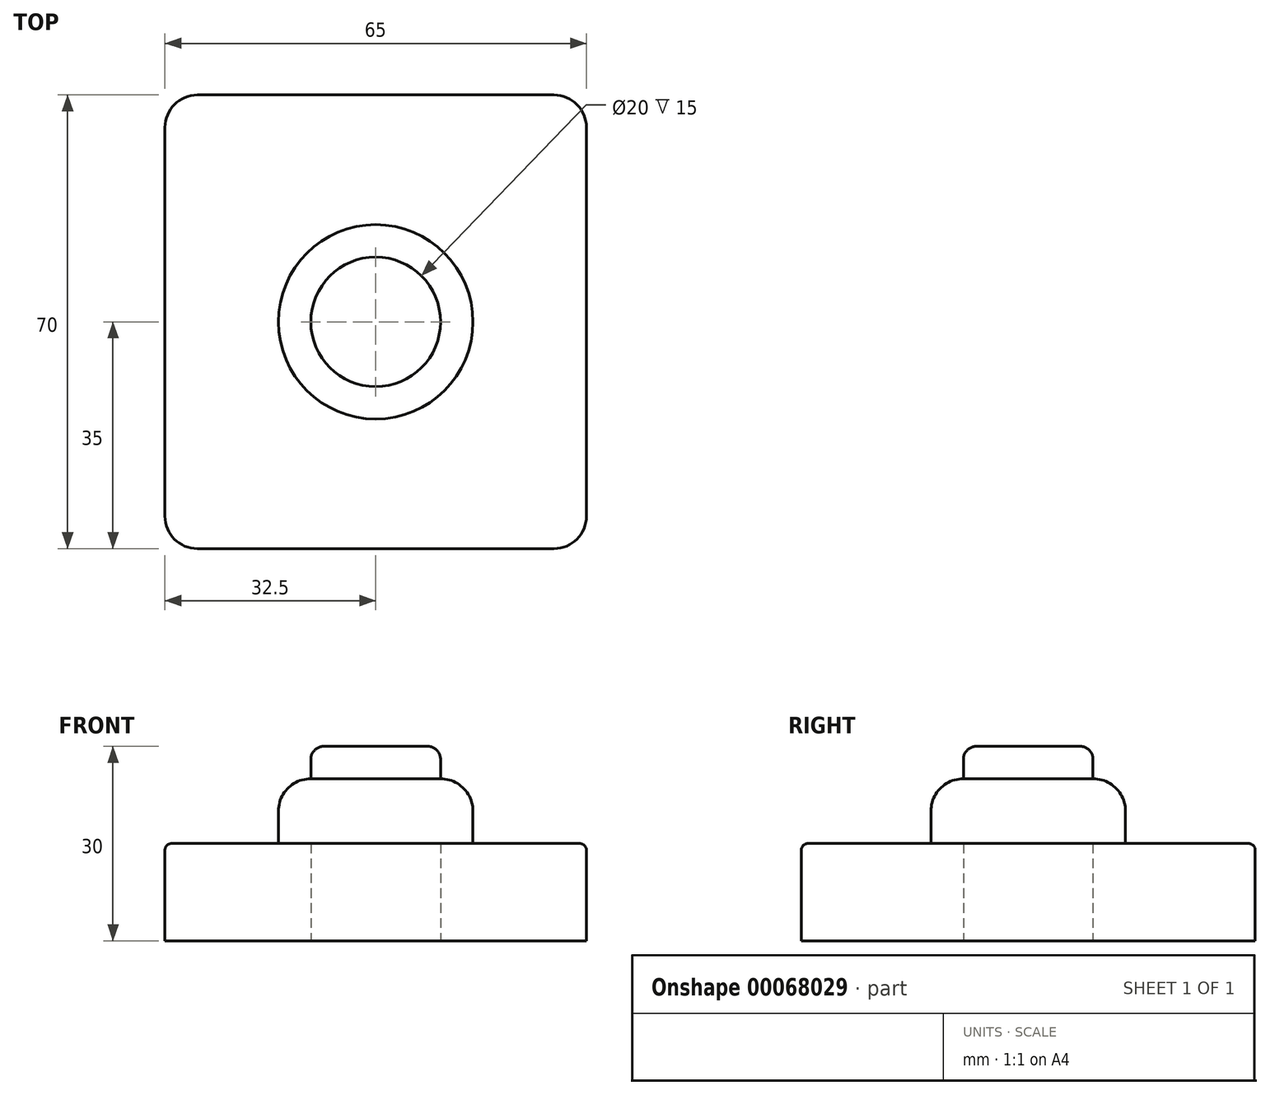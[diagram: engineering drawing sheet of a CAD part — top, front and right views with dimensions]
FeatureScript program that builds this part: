
annotation { "Feature Type Name" : "Feature", "Feature Type Description" : "" }
export const myFeature = defineFeature(function(context is Context, id is Id, definition is map)
    precondition{}
    {
        {
            var Q0;
            Q0=qCreatedBy(makeId("Top.planeOp"),FACE);
            var sketch = newSketch(context, id + "F0", { "sketchPlane" : qUnion([Q0])});
            skLineSegment(sketch, "E0.bottom", {"start": v(-27.5, 35) * mm, "end": v(27.5, 35) * mm});
            skLineSegment(sketch, "E0.top", {"start": v(-27.5, -35) * mm, "end": v(27.5, -35) * mm});
            skLineSegment(sketch, "E0.left", {"start": v(-32.5, 30) * mm, "end": v(-32.5, -30) * mm});
            skLineSegment(sketch, "E0.right", {"start": v(32.5, 30) * mm, "end": v(32.5, -30) * mm});
            skCircle(sketch, "E1", {"center": v(0, 0) * mm, "radius": 10 * mm});
            skPoint(sketch, "E2.visualSharp", {"position": v(-32.5, 35) * mm});
            skArc(sketch, "E2.filletArc", {"start": v(-27.5, 35) * mm, "mid": v(-31.04, 33.54) * mm, "end": v(-32.5, 30) * mm});
            skPoint(sketch, "E3.visualSharp", {"position": v(-32.5, -35) * mm});
            skArc(sketch, "E3.filletArc", {"start": v(-32.5, -30) * mm, "mid": v(-31.04, -33.54) * mm, "end": v(-27.5, -35) * mm});
            skPoint(sketch, "E4.visualSharp", {"position": v(32.5, -35) * mm});
            skArc(sketch, "E4.filletArc", {"start": v(27.5, -35) * mm, "mid": v(31.04, -33.54) * mm, "end": v(32.5, -30) * mm});
            skPoint(sketch, "E5.visualSharp", {"position": v(32.5, 35) * mm});
            skArc(sketch, "E5.filletArc", {"start": v(32.5, 30) * mm, "mid": v(31.04, 33.54) * mm, "end": v(27.5, 35) * mm});
            skSolve(sketch);
        }
        {
            var Q0;
            Q0 = qSketchRegion(id + "F0", true);
            extrude(context, id + "F1", {"entities" : qUnion([Q0]), "flatOperationType" : FlatOperationType.REMOVE, "depth" : 15 * mm, "offsetDistance" : 25 * mm, "domain" : OperationDomain.MODEL});
        }
        {
            var Q0;
            Q0=makeQuery(id+"F1.opExtrude","CAP_FACE",FACE,{"disambiguationData":[OSD([sQuery(id+"F0.wireOp",EDGE,"E0.bottom"),sQuery(id+"F0.wireOp",EDGE,"E0.top"),sQuery(id+"F0.wireOp",EDGE,"E0.left"),sQuery(id+"F0.wireOp",EDGE,"E0.right")])],"isStart":false});
            var sketch = newSketch(context, id + "F2", { "sketchPlane" : qUnion([Q0])});
            skCircle(sketch, "E6", {"center": v(0, 0) * mm, "radius": 15 * mm});
            skSolve(sketch);
        }
        {
            var Q0;
            Q0 = qSketchRegion(id + "F2", true);
            extrude(context, id + "F3", {"entities" : qUnion([Q0]), "operationType" : NewBodyOperationType.ADD, "depth" : 10 * mm});
        }
        {
            var Q0;
            Q0=makeQuery(id+"F3.opExtrude","CAP_EDGE",EDGE,{"disambiguationData":[OSD([sQuery(id+"F2.wireOp",EDGE,"E6")])],"isStart":false});
            fillet(context, id + "F4", {"entities" : qUnion([Q0]), "radius" : 5 * mm, "tangentPropagation" : true, "allowEdgeOverflow" : false});
        }
        {
            var Q0;
            Q0=makeQuery(id+"F1.opExtrude","CAP_EDGE",EDGE,{"disambiguationData":[OSD([sQuery(id+"F0.wireOp",EDGE,"E0.bottom")])],"isStart":false});
            var Q1;
            Q1=makeQuery(id+"F1.opExtrude","CAP_EDGE",EDGE,{"disambiguationData":[OSD([sQuery(id+"F0.wireOp",EDGE,"E5.filletArc")])],"isStart":false});
            var Q2;
            Q2=makeQuery(id+"F1.opExtrude","CAP_EDGE",EDGE,{"disambiguationData":[OSD([sQuery(id+"F0.wireOp",EDGE,"E0.right")])],"isStart":false});
            var Q3;
            Q3=makeQuery(id+"F1.opExtrude","CAP_EDGE",EDGE,{"disambiguationData":[OSD([sQuery(id+"F0.wireOp",EDGE,"E0.top")])],"isStart":false});
            var Q4;
            Q4=makeQuery(id+"F1.opExtrude","CAP_EDGE",EDGE,{"disambiguationData":[OSD([sQuery(id+"F0.wireOp",EDGE,"E4.filletArc")])],"isStart":false});
            var Q5;
            Q5=makeQuery(id+"F1.opExtrude","CAP_EDGE",EDGE,{"disambiguationData":[OSD([sQuery(id+"F0.wireOp",EDGE,"E3.filletArc")])],"isStart":false});
            var Q6;
            Q6=makeQuery(id+"F1.opExtrude","CAP_EDGE",EDGE,{"disambiguationData":[OSD([sQuery(id+"F0.wireOp",EDGE,"E0.left")])],"isStart":false});
            var Q7;
            Q7=makeQuery(id+"F1.opExtrude","CAP_EDGE",EDGE,{"disambiguationData":[OSD([sQuery(id+"F0.wireOp",EDGE,"E2.filletArc")])],"isStart":false});
            fillet(context, id + "F5", {"entities" : qUnion([Q0, Q1, Q2, Q3, Q4, Q5, Q6, Q7]), "radius" : 1 * mm, "tangentPropagation" : true, "allowEdgeOverflow" : false});
        }
        {
            var Q0;
            Q0=makeQuery(id+"F3.opExtrude","CAP_FACE",FACE,{"disambiguationData":[OSD([sQuery(id+"F2.wireOp",EDGE,"E6")])],"isStart":false});
            extrude(context, id + "F6", {"entities" : qUnion([Q0]), "operationType" : NewBodyOperationType.ADD, "flatOperationType" : FlatOperationType.REMOVE, "depth" : 5 * mm, "offsetDistance" : 25 * mm, "domain" : OperationDomain.MODEL});
        }
        {
            var Q0;
            Q0=makeQuery(id+"F6.opExtrude","CAP_EDGE",EDGE,{"disambiguationData":[OSD([sQuery(id+"F2.wireOp",EDGE,"E6")])],"isStart":false});
            fillet(context, id + "F7", {"entities" : qUnion([Q0]), "radius" : 2 * mm, "tangentPropagation" : true, "defaultsChanged" : true, "vertexSettings" : [], "allowEdgeOverflow" : false});
        }
    });
